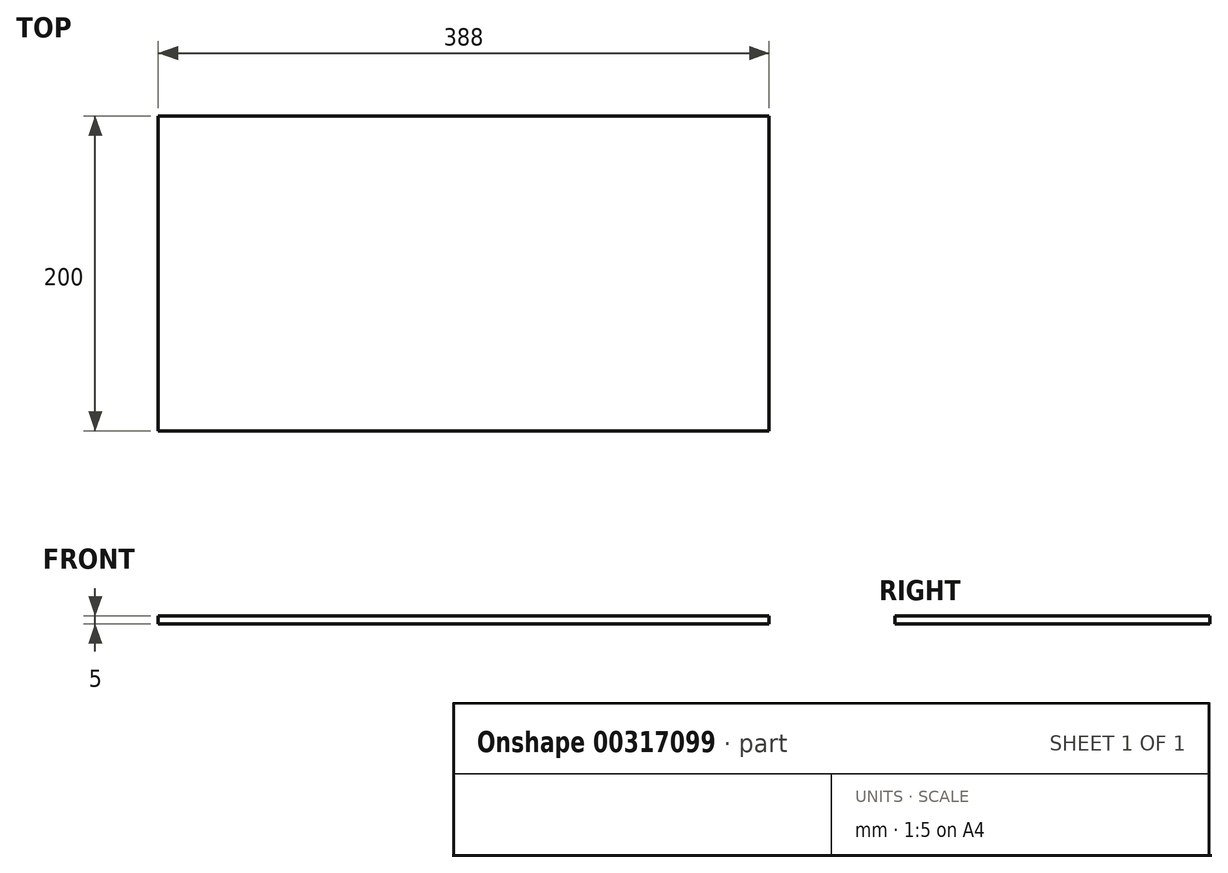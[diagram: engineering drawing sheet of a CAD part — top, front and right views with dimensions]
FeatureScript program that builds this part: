
annotation { "Feature Type Name" : "Feature", "Feature Type Description" : "" }
export const myFeature = defineFeature(function(context is Context, id is Id, definition is map)
    precondition{}
    {
        {
            var Q0;
            Q0=qCreatedBy(makeId("Top.planeOp"),FACE);
            var sketch = newSketch(context, id + "F0", { "sketchPlane" : qUnion([Q0])});
            skLineSegment(sketch, "E0.bottom", {"start": v(-194, 100) * mm, "end": v(194, 100) * mm});
            skLineSegment(sketch, "E0.top", {"start": v(-194, -100) * mm, "end": v(194, -100) * mm});
            skLineSegment(sketch, "E0.left", {"start": v(-194, 100) * mm, "end": v(-194, -100) * mm});
            skLineSegment(sketch, "E0.right", {"start": v(194, 100) * mm, "end": v(194, -100) * mm});
            skPoint(sketch, "E0.middle", {"position": v(0, 0) * mm});
            skSolve(sketch);
        }
        {
            var Q0;
            Q0=makeQuery(id+"F0.imprint","IMPRINT",FACE,{"disambiguationData":[TD([[makeQuery(id+"F0.imprint","IMPRINT",EDGE,{"derivedFrom":sQuery(id+"F0.wireOp",EDGE,"E0.bottom")}),-1.0]])]});
            extrude(context, id + "F1", {"entities" : qUnion([Q0]), "oppositeDirection" : true, "depth" : 5 * mm});
        }
    });
